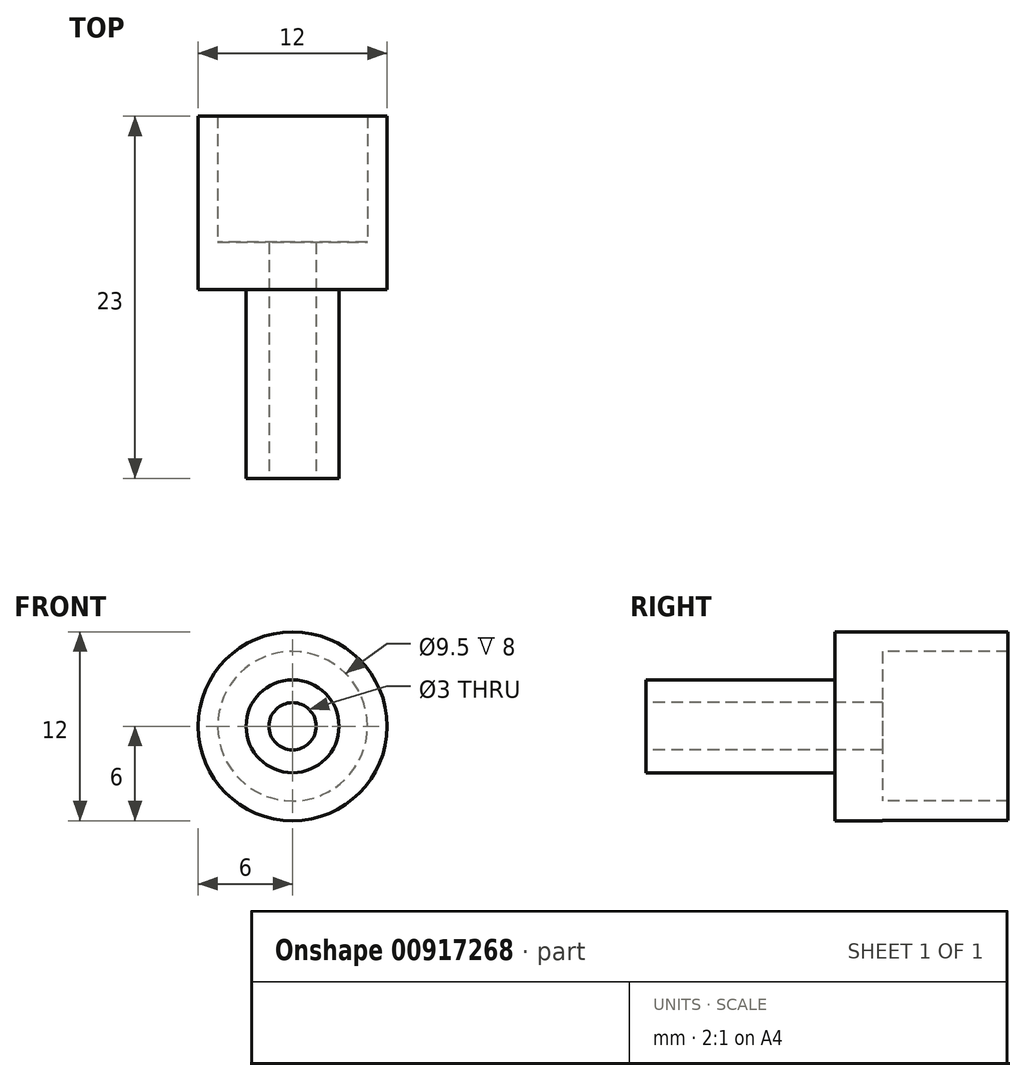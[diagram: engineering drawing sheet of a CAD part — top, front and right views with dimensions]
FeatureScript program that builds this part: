
annotation { "Feature Type Name" : "Feature", "Feature Type Description" : "" }
export const myFeature = defineFeature(function(context is Context, id is Id, definition is map)
    precondition{}
    {
        {
            var Q0;
            Q0=qCreatedBy(makeId("Front.planeOp"),FACE);
            var sketch = newSketch(context, id + "F0", { "sketchPlane" : qUnion([Q0])});
            skCircle(sketch, "E0", {"center": v(0, 0) * mm, "radius": 2.95 * mm});
            skSolve(sketch);
        }
        {
            var Q0;
            Q0 = qSketchRegion(id + "F0", true);
            var Q1;
            Q1=makeQuery(id+"F0.imprint","IMPRINT",FACE,{"disambiguationData":[TD([[makeQuery(id+"F0.imprint","IMPRINT",EDGE,{"derivedFrom":sQuery(id+"F0.wireOp",EDGE,"E0")}),1.0]])]});
            extrude(context, id + "F1", {"entities" : qUnion([Q0, Q1]), "depth" : 12 * mm, "offsetDistance" : 25 * mm});
        }
        {
            var Q0;
            Q0=makeQuery(id+"F1.opExtrude","CAP_FACE",FACE,{"disambiguationData":[OSD([sQuery(id+"F0.wireOp",EDGE,"E0")])],"isStart":true});
            var sketch = newSketch(context, id + "F2", { "sketchPlane" : qUnion([Q0])});
            skCircle(sketch, "E1", {"center": v(0, 0) * mm, "radius": 6 * mm});
            skSolve(sketch);
        }
        {
            var Q0;
            Q0=makeQuery(id+"F2.imprint","IMPRINT",FACE,{"disambiguationData":[TD([[makeQuery(id+"F2.imprint","IMPRINT",EDGE,{"derivedFrom":makeQuery(id+"F1.opExtrude","CAP_EDGE",EDGE,{"disambiguationData":[OSD([sQuery(id+"F0.wireOp",EDGE,"E0")])],"isStart":true})}),-1.0]])]});
            var Q1;
            Q1=makeQuery(id+"F2.imprint","IMPRINT",FACE,{"disambiguationData":[TD([[makeQuery(id+"F2.imprint","IMPRINT",EDGE,{"derivedFrom":sQuery(id+"F2.wireOp",EDGE,"E1")}),1.0]])]});
            extrude(context, id + "F3", {"entities" : qUnion([Q0, Q1]), "operationType" : NewBodyOperationType.ADD, "depth" : 3 * mm, "offsetDistance" : 25 * mm});
        }
        {
            var Q0;
            Q0=makeQuery(id+"F3.opExtrude","CAP_FACE",FACE,{"disambiguationData":[OSD([sQuery(id+"F2.wireOp",EDGE,"E1")])],"isStart":false});
            var sketch = newSketch(context, id + "F4", { "sketchPlane" : qUnion([Q0])});
            skCircle(sketch, "E2", {"center": v(0, 0) * mm, "radius": 4.75 * mm});
            skCircle(sketch, "E3", {"center": v(0, 0) * mm, "radius": 6 * mm});
            skSolve(sketch);
        }
        {
            var Q0;
            Q0=makeQuery(id+"F4.imprint","IMPRINT",FACE,{"disambiguationData":[TD([[makeQuery(id+"F4.imprint","IMPRINT",EDGE,{"derivedFrom":sQuery(id+"F4.wireOp",EDGE,"E2")}),-1.0]])]});
            extrude(context, id + "F5", {"entities" : qUnion([Q0]), "operationType" : NewBodyOperationType.ADD, "depth" : 8 * mm, "offsetDistance" : 25 * mm});
        }
        {
            var Q0;
            Q0=makeQuery(id+"F1.opExtrude","CAP_FACE",FACE,{"disambiguationData":[OSD([sQuery(id+"F0.wireOp",EDGE,"E0")])],"isStart":false});
            var sketch = newSketch(context, id + "F6", { "sketchPlane" : qUnion([Q0])});
            skCircle(sketch, "E4", {"center": v(0, 0) * mm, "radius": 1.5 * mm});
            skSolve(sketch);
        }
        {
            var Q0;
            Q0=makeQuery(id+"F6.imprint","IMPRINT",FACE,{"disambiguationData":[TD([[makeQuery(id+"F6.imprint","IMPRINT",EDGE,{"derivedFrom":sQuery(id+"F6.wireOp",EDGE,"E4")}),1.0]])]});
            extrude(context, id + "F7", {"entities" : qUnion([Q0]), "operationType" : NewBodyOperationType.REMOVE, "oppositeDirection" : true, "depth" : 25 * mm, "offsetDistance" : 25 * mm});
        }
    });
